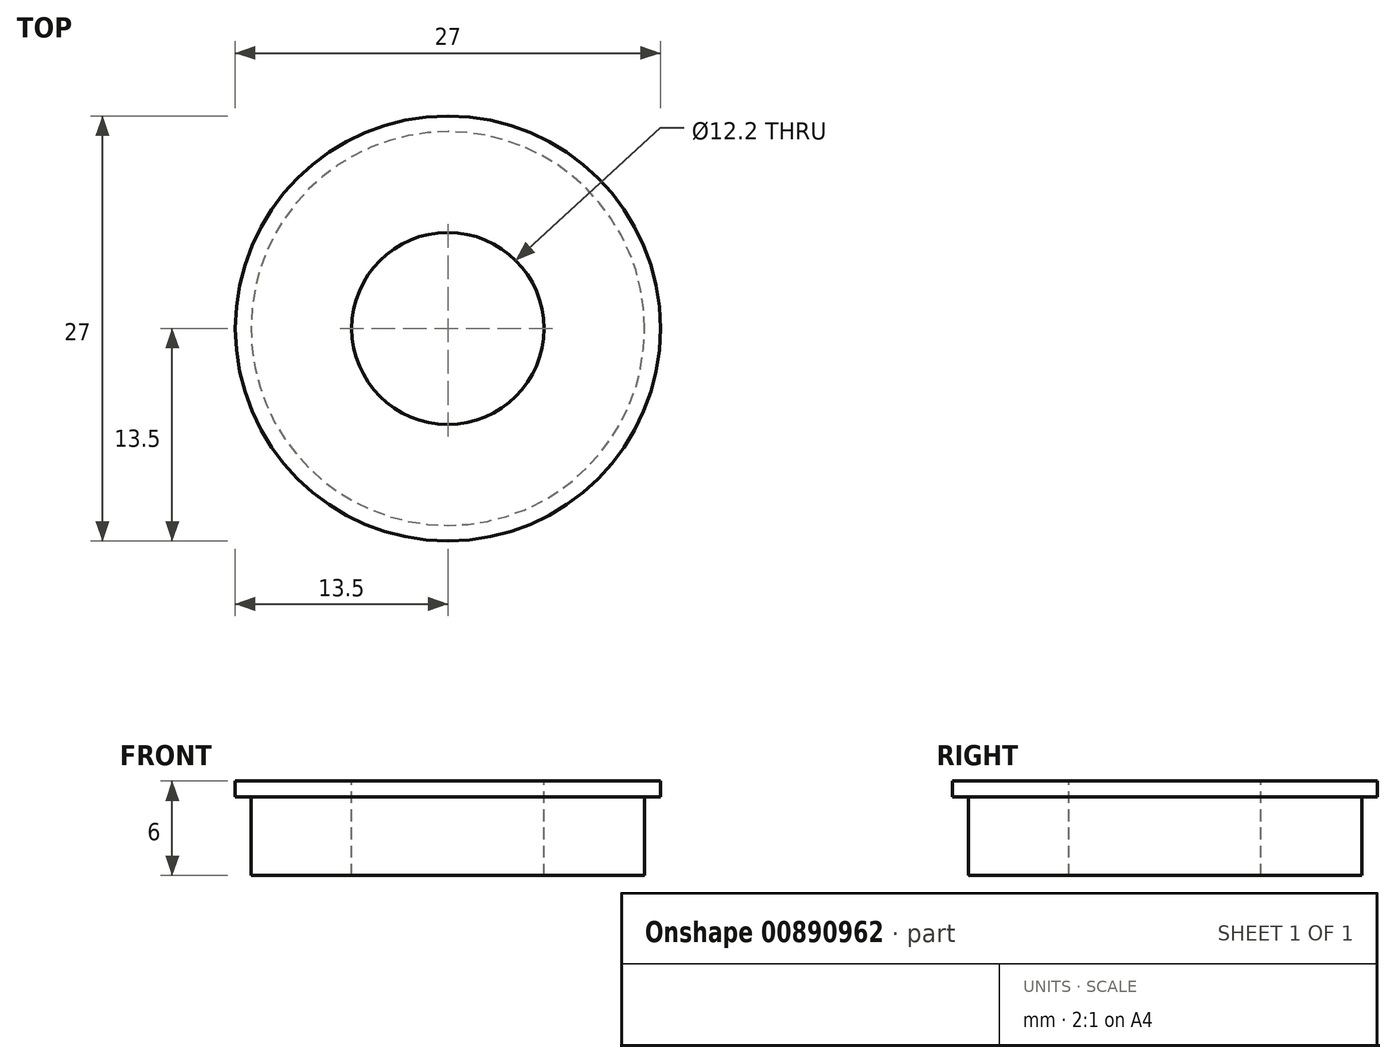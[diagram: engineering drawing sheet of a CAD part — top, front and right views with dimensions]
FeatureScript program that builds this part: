
annotation { "Feature Type Name" : "Feature", "Feature Type Description" : "" }
export const myFeature = defineFeature(function(context is Context, id is Id, definition is map)
    precondition{}
    {
        {
            var Q0;
            Q0=qCreatedBy(makeId("Top.planeOp"),FACE);
            var sketch = newSketch(context, id + "F0", { "sketchPlane" : qUnion([Q0])});
            skCircle(sketch, "E0", {"center": v(0, 0) * mm, "radius": 13.5 * mm});
            skSolve(sketch);
        }
        {
            var Q0;
            Q0=qSketchRegion(id+"F0",true);
            extrude(context, id + "F1", {"entities" : qUnion([Q0]), "depth" : 1 * mm, "offsetDistance" : 25 * mm});
        }
        {
            var Q0;
            Q0=makeQuery(id+"F1.opExtrude","CAP_FACE",FACE,{"disambiguationData":[OSD([sQuery(id+"F0.wireOp",EDGE,"E0")])],"isStart":true});
            var sketch = newSketch(context, id + "F2", { "sketchPlane" : qUnion([Q0])});
            skCircle(sketch, "E1", {"center": v(0, 0) * mm, "radius": 12.5 * mm});
            skSolve(sketch);
        }
        {
            var Q0;
            Q0=qSketchRegion(id+"F2",true);
            extrude(context, id + "F3", {"entities" : qUnion([Q0]), "operationType" : NewBodyOperationType.ADD, "depth" : 5 * mm, "offsetDistance" : 25 * mm});
        }
        {
            var Q0;
            Q0=makeQuery(id+"F1.opExtrude","CAP_FACE",FACE,{"disambiguationData":[OSD([sQuery(id+"F0.wireOp",EDGE,"E0")])],"isStart":false});
            var sketch = newSketch(context, id + "F4", { "sketchPlane" : qUnion([Q0])});
            skCircle(sketch, "E2", {"center": v(0, 0) * mm, "radius": 6.1 * mm});
            skSolve(sketch);
        }
        {
            var Q0;
            Q0 = qSketchRegion(id + "F4", true);
            extrude(context, id + "F5", {"entities" : qUnion([Q0]), "operationType" : NewBodyOperationType.REMOVE, "endBound" : BoundingType.THROUGH_ALL, "oppositeDirection" : true, "depth" : 25 * mm, "offsetDistance" : 25 * mm});
        }
    });
